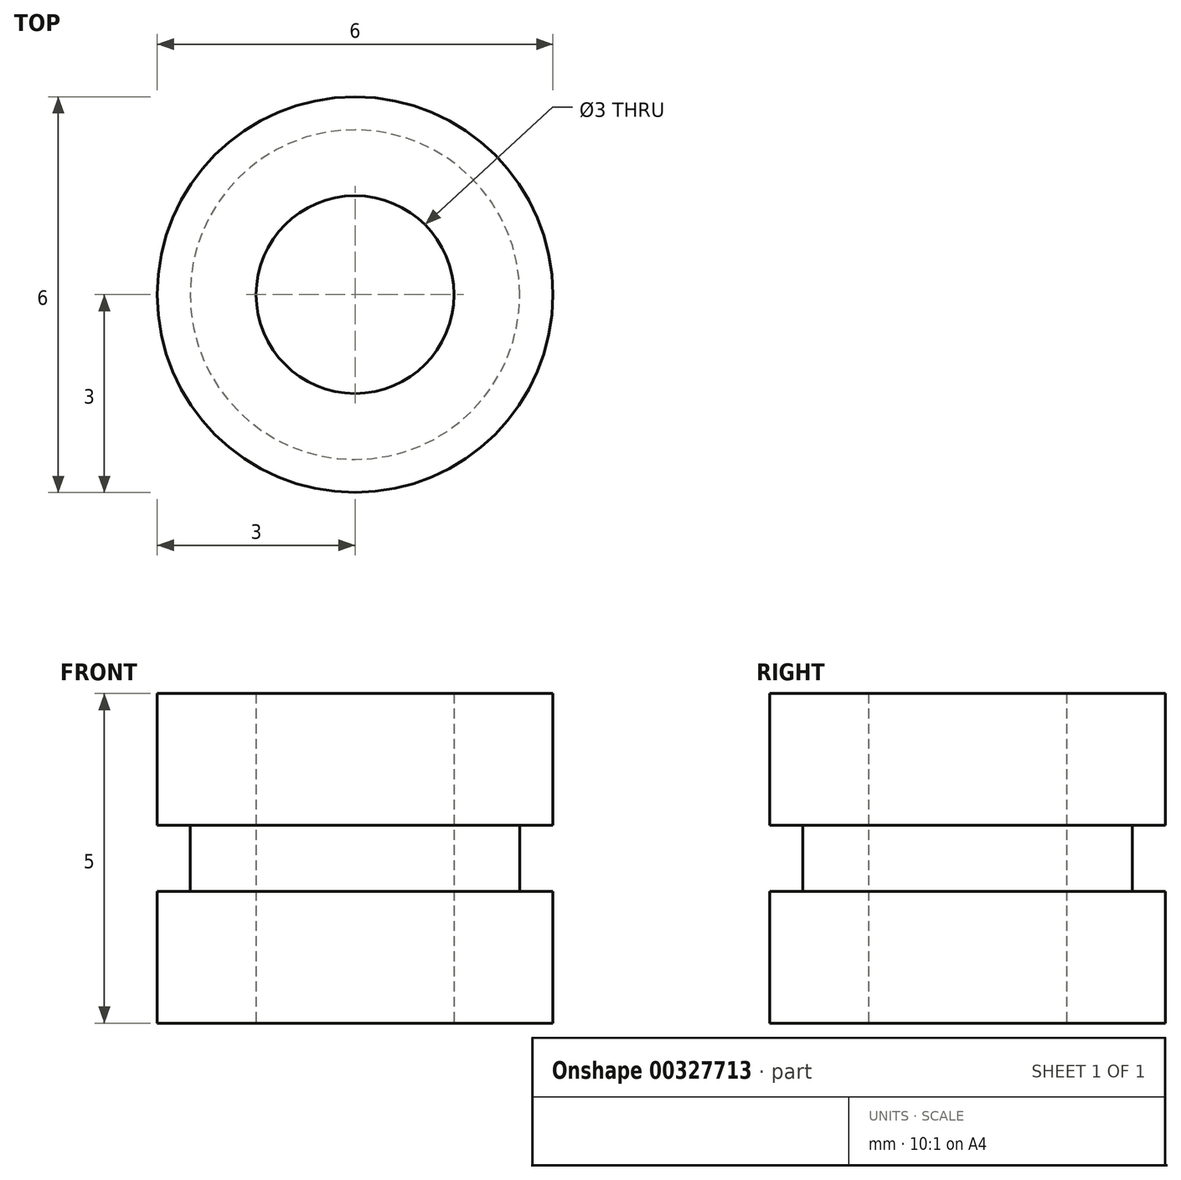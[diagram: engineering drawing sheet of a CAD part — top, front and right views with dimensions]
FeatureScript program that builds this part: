
annotation { "Feature Type Name" : "Feature", "Feature Type Description" : "" }
export const myFeature = defineFeature(function(context is Context, id is Id, definition is map)
    precondition{}
    {
        {
            var Q0;
            Q0=qCreatedBy(makeId("Top.planeOp"),FACE);
            var sketch = newSketch(context, id + "F0", { "sketchPlane" : qUnion([Q0])});
            skCircle(sketch, "E0", {"center": v(0, 0) * mm, "radius": 1.5 * mm});
            skCircle(sketch, "E1", {"center": v(0, 0) * mm, "radius": 2.5 * mm});
            skCircle(sketch, "E2", {"center": v(0, 0) * mm, "radius": 3 * mm});
            skSolve(sketch);
        }
        {
            var Q0;
            Q0=makeQuery(id+"F0.imprint","IMPRINT",FACE,{"disambiguationData":[TD([[makeQuery(id+"F0.imprint","IMPRINT",EDGE,{"derivedFrom":sQuery(id+"F0.wireOp",EDGE,"E0")}),-1.0]])]});
            extrude(context, id + "F1", {"entities" : qUnion([Q0]), "depth" : 5 * mm});
        }
        {
            var Q0;
            Q0=qSketchRegion(id+"F0",true);
            extrude(context, id + "F2", {"entities" : qUnion([Q0]), "operationType" : NewBodyOperationType.ADD, "depth" : 2 * mm});
        }
        {
            var Q0;
            Q0=makeQuery(id+"F1.opExtrude","CAP_FACE",FACE,{"disambiguationData":[OSD([sQuery(id+"F0.wireOp",EDGE,"E0"),sQuery(id+"F0.wireOp",EDGE,"E1")])],"isStart":false});
            var sketch = newSketch(context, id + "F3", { "sketchPlane" : qUnion([Q0])});
            skCircle(sketch, "E3", {"center": v(0, 0) * mm, "radius": 3 * mm});
            skSolve(sketch);
        }
        {
            var Q0;
            Q0=makeQuery(id+"F3.imprint","IMPRINT",FACE,{"disambiguationData":[TD([[makeQuery(id+"F3.imprint","IMPRINT",EDGE,{"derivedFrom":sQuery(id+"F3.wireOp",EDGE,"E3")}),1.0]])]});
            extrude(context, id + "F4", {"entities" : qUnion([Q0]), "operationType" : NewBodyOperationType.ADD, "oppositeDirection" : true, "depth" : 2 * mm});
        }
    });
